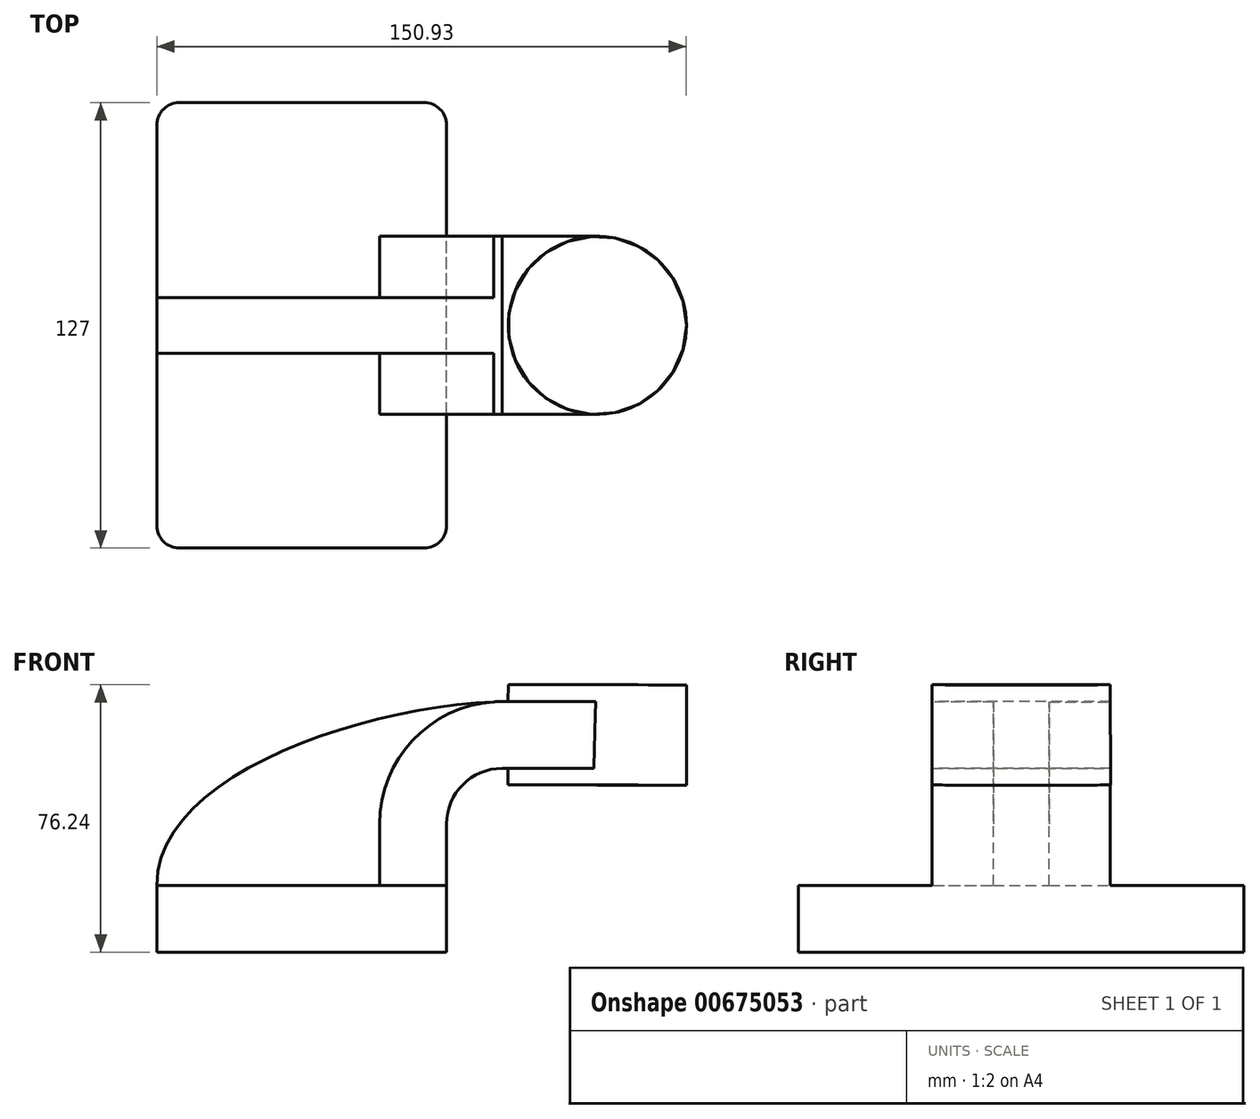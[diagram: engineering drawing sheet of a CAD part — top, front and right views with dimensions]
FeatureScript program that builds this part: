
annotation { "Feature Type Name" : "Feature", "Feature Type Description" : "" }
export const myFeature = defineFeature(function(context is Context, id is Id, definition is map)
    precondition{}
    {
        {
            var Q0;
            Q0=qCreatedBy(makeId("Front.planeOp"),FACE);
            var sketch = newSketch(context, id + "F0", { "sketchPlane" : qUnion([Q0])});
            skLineSegment(sketch, "E0.bottom", {"start": v(41.27, 9.53) * mm, "end": v(-41.28, 9.53) * mm});
            skLineSegment(sketch, "E0.top", {"start": v(41.28, -9.52) * mm, "end": v(-41.27, -9.52) * mm});
            skLineSegment(sketch, "E0.left", {"start": v(41.28, 9.53) * mm, "end": v(41.28, -9.52) * mm});
            skLineSegment(sketch, "E0.right", {"start": v(-41.28, 9.53) * mm, "end": v(-41.27, -9.52) * mm});
            skPoint(sketch, "E0.middle", {"position": v(0, 0) * mm});
            skLineSegment(sketch, "E1.bottom", {"start": v(109.65, 66.68) * mm, "end": v(58.85, 66.68) * mm});
            skLineSegment(sketch, "E1.top", {"start": v(109.65, 38.1) * mm, "end": v(58.85, 38.1) * mm});
            skLineSegment(sketch, "E1.left", {"start": v(109.65, 66.68) * mm, "end": v(109.65, 38.1) * mm});
            skLineSegment(sketch, "E1.right", {"start": v(58.85, 66.68) * mm, "end": v(58.85, 38.1) * mm});
            skPoint(sketch, "E1.middle", {"position": v(84.25, 52.39) * mm});
            skLineSegment(sketch, "E2", {"start": v(41.27, 9.53) * mm, "end": v(41.27, 27) * mm});
            skArc(sketch, "E3", {"start": v(41.27, 27) * mm, "mid": v(45.92, 38.23) * mm, "end": v(57.15, 42.88) * mm});
            skLineSegment(sketch, "E4", {"start": v(57.15, 42.88) * mm, "end": v(84.23, 42.88) * mm});
            skLineSegment(sketch, "E5.0", {"start": v(57.15, 61.93) * mm, "end": v(84.23, 61.93) * mm});
            skArc(sketch, "E5.1", {"start": v(22.23, 27) * mm, "mid": v(32.45, 51.7) * mm, "end": v(57.15, 61.93) * mm});
            skLineSegment(sketch, "E5.2", {"start": v(22.22, 9.53) * mm, "end": v(22.22, 27) * mm});
            skFitSpline(sketch, "E6", {"points": [v(-41.28, 9.52) * mm, v(57.15, 61.93) * mm], "startDerivative": vector(-1.04, 94.8) * mm, "endDerivative": vector(116.8, 2.87) * mm});
            skLineSegment(sketch, "E7", {"start": v(84.23, 61.93) * mm, "end": v(84.23, 42.88) * mm});
            skLineSegment(sketch, "E8", {"start": v(84.25, 66.68) * mm, "end": v(84.23, 38.1) * mm});
            skSolve(sketch);
        }
        {
            var Q0;
            Q0=makeQuery(id+"F0.imprint","IMPRINT",FACE,{"disambiguationData":[TD([[makeQuery(id+"F0.imprint","IMPRINT",EDGE,{"derivedFrom":sQuery(id+"F0.wireOp",EDGE,"E0.top")}),-1.0]])]});
            extrude(context, id + "F1", {"entities" : qUnion([Q0]), "endBound" : BoundingType.SYMMETRIC, "depth" : 127 * mm, "offsetDistance" : 25.4 * mm});
        }
        {
            var Q0;
            {var subQ1=sQuery(id+"F0.wireOp",EDGE,"E2");Q0=makeQuery(id+"F0.imprint","IMPRINT",FACE,{"disambiguationData":[TD([[makeQuery(id+"F0.imprint","IMPRINT",EDGE,{"derivedFrom":subQ1}),1.0]])]});}
            var Q1;
            {var subQ5=sQuery(id+"F0.wireOp",EDGE,"E7");Q1=makeQuery(id+"F0.imprint","IMPRINT",FACE,{"disambiguationData":[TD([[makeQuery(id+"F0.imprint","IMPRINT",EDGE,{"derivedFrom":subQ5}),-1.0]])]});}
            extrude(context, id + "F2", {"entities" : qUnion([Q0, Q1]), "operationType" : NewBodyOperationType.ADD, "endBound" : BoundingType.SYMMETRIC, "depth" : 50.8 * mm, "offsetDistance" : 25.4 * mm});
        }
        {
            var Q0;
            {var subQ3=sQuery(id+"F0.wireOp",EDGE,"E5.2");Q0=makeQuery(id+"F0.imprint","IMPRINT",FACE,{"disambiguationData":[TD([[makeQuery(id+"F0.imprint","IMPRINT",EDGE,{"derivedFrom":subQ3}),1.0]])]});}
            extrude(context, id + "F3", {"entities" : qUnion([Q0]), "operationType" : NewBodyOperationType.ADD, "endBound" : BoundingType.SYMMETRIC, "depth" : 15.88 * mm, "offsetDistance" : 25.4 * mm});
        }
        {
            var Q0;
            {var subQ0=sQuery(id+"F0.wireOp",EDGE,"E1.left");Q0=makeQuery(id+"F0.imprint","IMPRINT",FACE,{"disambiguationData":[TD([[makeQuery(id+"F0.imprint","IMPRINT",EDGE,{"derivedFrom":subQ0}),-1.0]])]});}
            var Q1;
            Q1=sQuery(id+"F0.wireOp",EDGE,"E8");
            revolve(context, id + "F4", {"operationType" : NewBodyOperationType.ADD, "entities" : qUnion([Q0]), "axis" : qUnion([Q1]), "revolveType" : RevolveType.FULL});
        }
        {
            var Q0;
            Q0=makeQuery(id+"F1.opExtrude","CAP_EDGE",EDGE,{"disambiguationData":[OSD([sQuery(id+"F0.wireOp",EDGE,"E0.left")])],"isStart":false});
            var Q1;
            Q1=makeQuery(id+"F1.opExtrude","CAP_EDGE",EDGE,{"disambiguationData":[OSD([sQuery(id+"F0.wireOp",EDGE,"E0.left")])],"isStart":true});
            var Q2;
            Q2=makeQuery(id+"F1.opExtrude","CAP_EDGE",EDGE,{"disambiguationData":[OSD([sQuery(id+"F0.wireOp",EDGE,"E0.right")])],"isStart":true});
            var Q3;
            Q3=makeQuery(id+"F1.opExtrude","CAP_EDGE",EDGE,{"disambiguationData":[OSD([sQuery(id+"F0.wireOp",EDGE,"E0.right")])],"isStart":false});
            fillet(context, id + "F5", {"entities" : qUnion([Q0, Q1, Q2, Q3]), "radius" : 6.35 * mm, "tangentPropagation" : true, "allowEdgeOverflow" : false});
        }
    });
